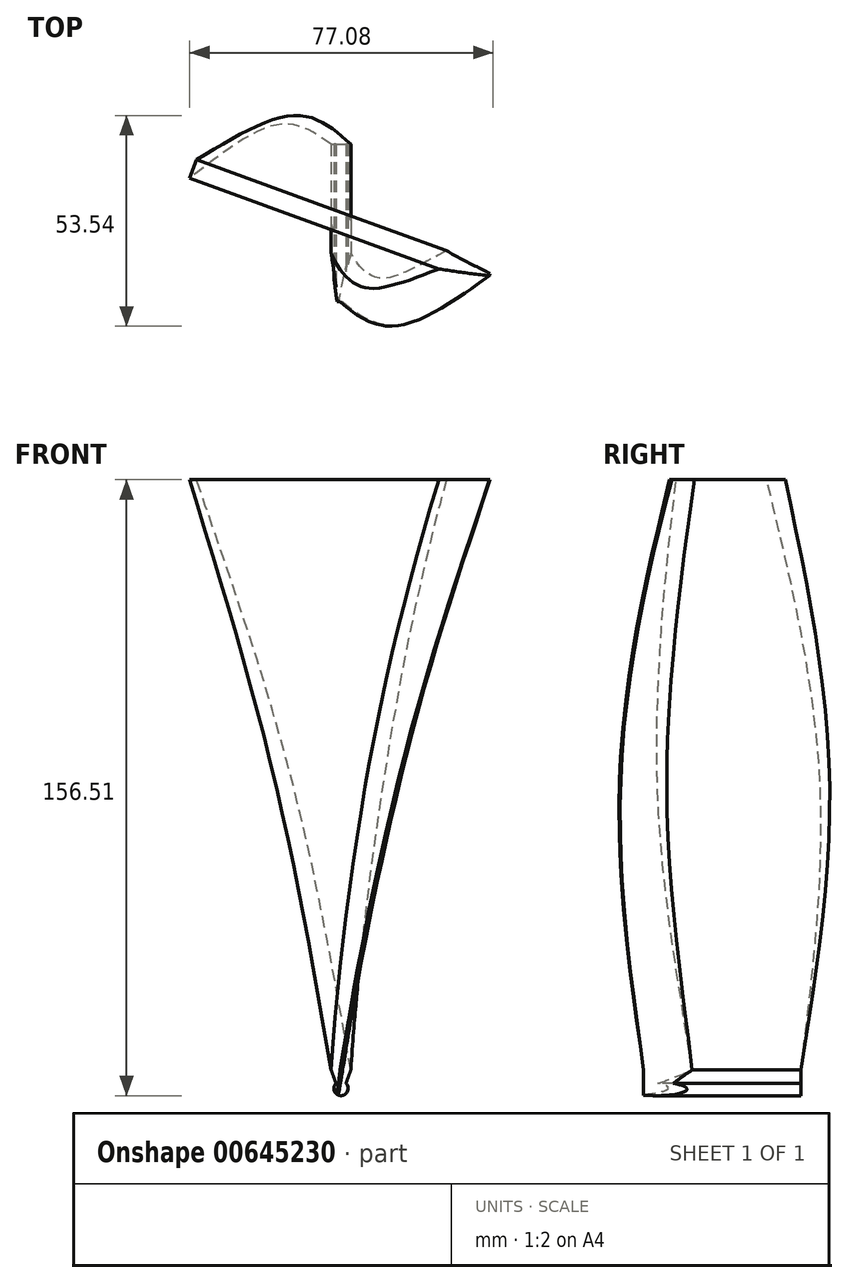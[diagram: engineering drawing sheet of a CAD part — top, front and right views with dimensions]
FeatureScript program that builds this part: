
annotation { "Feature Type Name" : "Feature", "Feature Type Description" : "" }
export const myFeature = defineFeature(function(context is Context, id is Id, definition is map)
    precondition{}
    {
        {
            var Q0;
            Q0=qCreatedBy(makeId("Top.planeOp"),FACE);
            var sketch = newSketch(context, id + "F0", { "sketchPlane" : qUnion([Q0])});
            skLineSegment(sketch, "E0.bottom", {"start": v(2.5, -20) * mm, "end": v(-2.5, -20) * mm});
            skLineSegment(sketch, "E0.top", {"start": v(2.5, 20) * mm, "end": v(-2.5, 20) * mm});
            skLineSegment(sketch, "E0.left", {"start": v(2.5, -20) * mm, "end": v(2.5, 20) * mm});
            skLineSegment(sketch, "E0.right", {"start": v(-2.5, -20) * mm, "end": v(-2.5, 20) * mm});
            skPoint(sketch, "E0.middle", {"position": v(0, 0) * mm});
            skSolve(sketch);
        }
        {
            var Q0;
            Q0=qCreatedBy(makeId("Top.planeOp"),FACE);
            cPlane(context, id + "F1", {"entities" : qUnion([Q0]), "cplaneType" : CPlaneType.OFFSET, "offset" : 75 * mm, "width" : 150 * mm, "height" : 150 * mm});
        }
        {
            var Q0;
            Q0=qCreatedBy(id+"F1.planeOp",FACE);
            var sketch = newSketch(context, id + "F2", { "sketchPlane" : qUnion([Q0])});
            skLineSegment(sketch, "E1.bottom", {"start": v(17.17, -24.73) * mm, "end": v(12.83, -27.23) * mm});
            skLineSegment(sketch, "E1.top", {"start": v(-12.83, 27.23) * mm, "end": v(-17.17, 24.73) * mm});
            skLineSegment(sketch, "E1.left", {"start": v(17.17, -24.73) * mm, "end": v(-12.83, 27.23) * mm});
            skLineSegment(sketch, "E1.right", {"start": v(12.83, -27.23) * mm, "end": v(-17.17, 24.73) * mm});
            skPoint(sketch, "E1.middle", {"position": v(0, 0) * mm});
            skLineSegment(sketch, "E2", {"start": v(-74.87, 0) * mm, "end": v(75.07, 0) * mm, "construction": true});
            skSolve(sketch);
        }
        {
            var Q0;
            Q0=qCreatedBy(id+"F1.planeOp",FACE);
            cPlane(context, id + "F3", {"entities" : qUnion([Q0]), "cplaneType" : CPlaneType.OFFSET, "offset" : 75 * mm, "width" : 150 * mm, "height" : 150 * mm});
        }
        {
            var Q0;
            Q0=qCreatedBy(id+"F3.planeOp",FACE);
            var sketch = newSketch(context, id + "F4", { "sketchPlane" : qUnion([Q0])});
            skLineSegment(sketch, "E3.bottom", {"start": v(38.44, -11.33) * mm, "end": v(36.73, -16.03) * mm});
            skLineSegment(sketch, "E3.top", {"start": v(-36.73, 16.03) * mm, "end": v(-38.44, 11.33) * mm});
            skLineSegment(sketch, "E3.left", {"start": v(38.44, -11.33) * mm, "end": v(-36.73, 16.03) * mm});
            skLineSegment(sketch, "E3.right", {"start": v(36.73, -16.03) * mm, "end": v(-38.44, 11.33) * mm});
            skPoint(sketch, "E3.middle", {"position": v(0, 0) * mm});
            skLineSegment(sketch, "E4", {"start": v(-74.98, 0) * mm, "end": v(75.2, 0) * mm, "construction": true});
            skSolve(sketch);
        }
        {
            var Q0;
            Q0=qCreatedBy(makeId("Front.planeOp"),FACE);
            var sketch = newSketch(context, id + "F5", { "sketchPlane" : qUnion([Q0])});
            skLineSegment(sketch, "E5.0", {"start": v(-2.5, 0) * mm, "end": v(2.5, 0) * mm});
            skLineSegment(sketch, "E6", {"start": v(-2.5, 0) * mm, "end": v(-1.26, -3.4) * mm});
            skLineSegment(sketch, "E7", {"start": v(2.5, 0) * mm, "end": v(1.26, -3.4) * mm});
            skLineSegment(sketch, "E8", {"start": v(-0.79, -4.7) * mm, "end": v(0.79, -4.7) * mm, "construction": true});
            skArc(sketch, "E9", {"start": v(-1.26, -3.4) * mm, "mid": v(0, -6.5) * mm, "end": v(1.26, -3.4) * mm});
            skSolve(sketch);
        }
        {
            var Q0;
            Q0=makeQuery(id+"F5.imprint","IMPRINT",FACE,{"disambiguationData":[TD([[makeQuery(id+"F5.imprint","IMPRINT",EDGE,{"derivedFrom":sQuery(id+"F5.wireOp",EDGE,"E5.0")}),-1.0]])]});
            var Q1;
            Q1=sQuery(id+"F0.wireOp",EDGE,"E0.right");
            sweep(context, id + "F6", {"profiles" : qUnion([Q0]), "path" : qUnion([Q1])});
        }
        {
            var Q1;
            Q1=makeQuery(id+"F0.imprint","IMPRINT",FACE,{"disambiguationData":[TD([[makeQuery(id+"F0.imprint","IMPRINT",EDGE,{"derivedFrom":sQuery(id+"F0.wireOp",EDGE,"E0.bottom")}),-1.0]])]});
            var Q2;
            Q2=makeQuery(id+"F2.imprint","IMPRINT",FACE,{"disambiguationData":[TD([[makeQuery(id+"F2.imprint","IMPRINT",EDGE,{"derivedFrom":sQuery(id+"F2.wireOp",EDGE,"E1.bottom")}),-1.0]])]});
            var Q3;
            Q3=makeQuery(id+"F4.imprint","IMPRINT",FACE,{"disambiguationData":[TD([[makeQuery(id+"F4.imprint","IMPRINT",EDGE,{"derivedFrom":sQuery(id+"F4.wireOp",EDGE,"E3.bottom")}),-1.0]])]});
            loft(context, id + "F7", {"operationType" : NewBodyOperationType.ADD, "sheetProfilesArray" : [{ "sheetProfileEntities" : qUnion([Q1]) }, { "sheetProfileEntities" : qUnion([Q2]) }, { "sheetProfileEntities" : qUnion([Q3]) }]});
        }
        {
            var Q0;
            Q0=makeQuery(id+"F7.opLoft","SWEPT_EDGE",EDGE,{"disambiguationData":[OSD([sQuery(id+"F0.wireOp",EDGE,"E0.bottom"),sQuery(id+"F0.wireOp",EDGE,"E0.right"),sQuery(id+"F2.wireOp",EDGE,"E1.bottom"),sQuery(id+"F2.wireOp",EDGE,"E1.right")])]});
            var Q1;
            Q1=makeQuery(id+"F7.opLoft","SWEPT_EDGE",EDGE,{"disambiguationData":[OSD([sQuery(id+"F0.wireOp",EDGE,"E0.bottom"),sQuery(id+"F0.wireOp",EDGE,"E0.left"),sQuery(id+"F2.wireOp",EDGE,"E1.bottom"),sQuery(id+"F2.wireOp",EDGE,"E1.left")])]});
            chamfer(context, id + "F8", {"entities" : qUnion([Q0, Q1]), "chamferType" : ChamferType.OFFSET_ANGLE, "width" : 2.5 * mm, "oppositeDirection" : true, "angle" : 80 * degree, "tangentPropagation" : true});
        }
    });
